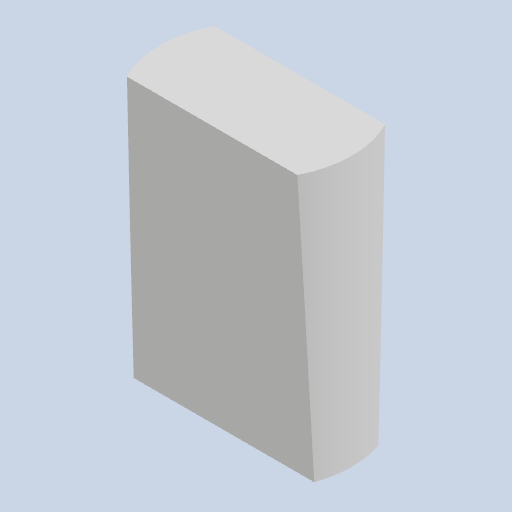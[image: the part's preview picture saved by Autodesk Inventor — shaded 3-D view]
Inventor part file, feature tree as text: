
AUTODESK INVENTOR PART (.ipt)
format: ipt  version: 2022 (Build 260153000, 153)  size: 119,296 bytes
history: native  units: mm
features: reference x12, other x5, extrude x2, sketch x2, projected_geometry x1
ambient origin geometry x8: Origin, YZ Plane, XZ Plane, XY Plane, X Axis, Y Axis, Z Axis, Center Point
bodies: Body1 (feature_tree)
feature tree (22):
  other  "Твердое тело1"
  extrude  "Выдавливание1"  Depth=0.436332mm
  extrude  "Выдавливание2"  Depth=0.15mm
  sketch  "Эскиз1"
  reference  "Ссылка1"
  reference  "Ссылка2"
  reference  "Ссылка3"
  reference  "Ссылка4"
  reference  "Ссылка5"
  reference  "Ссылка6"
  reference  "Ссылка7"
  reference  "Ссылка8"
  sketch  "Эскиз2"
  reference  "Ссылка9"
  reference  "Ссылка10"
  projected_geometry  "Спроецированная петля1"
  reference  "Ссылка11"
  reference  "Ссылка12"
  other  "<userpath>\Documents\Git\MZCAT_2024\MZCAT_4.iam"
  other  "MZCAT_4.iam"
  other  "middle_gear_vtulka:1"
  other  "base plate:1"
